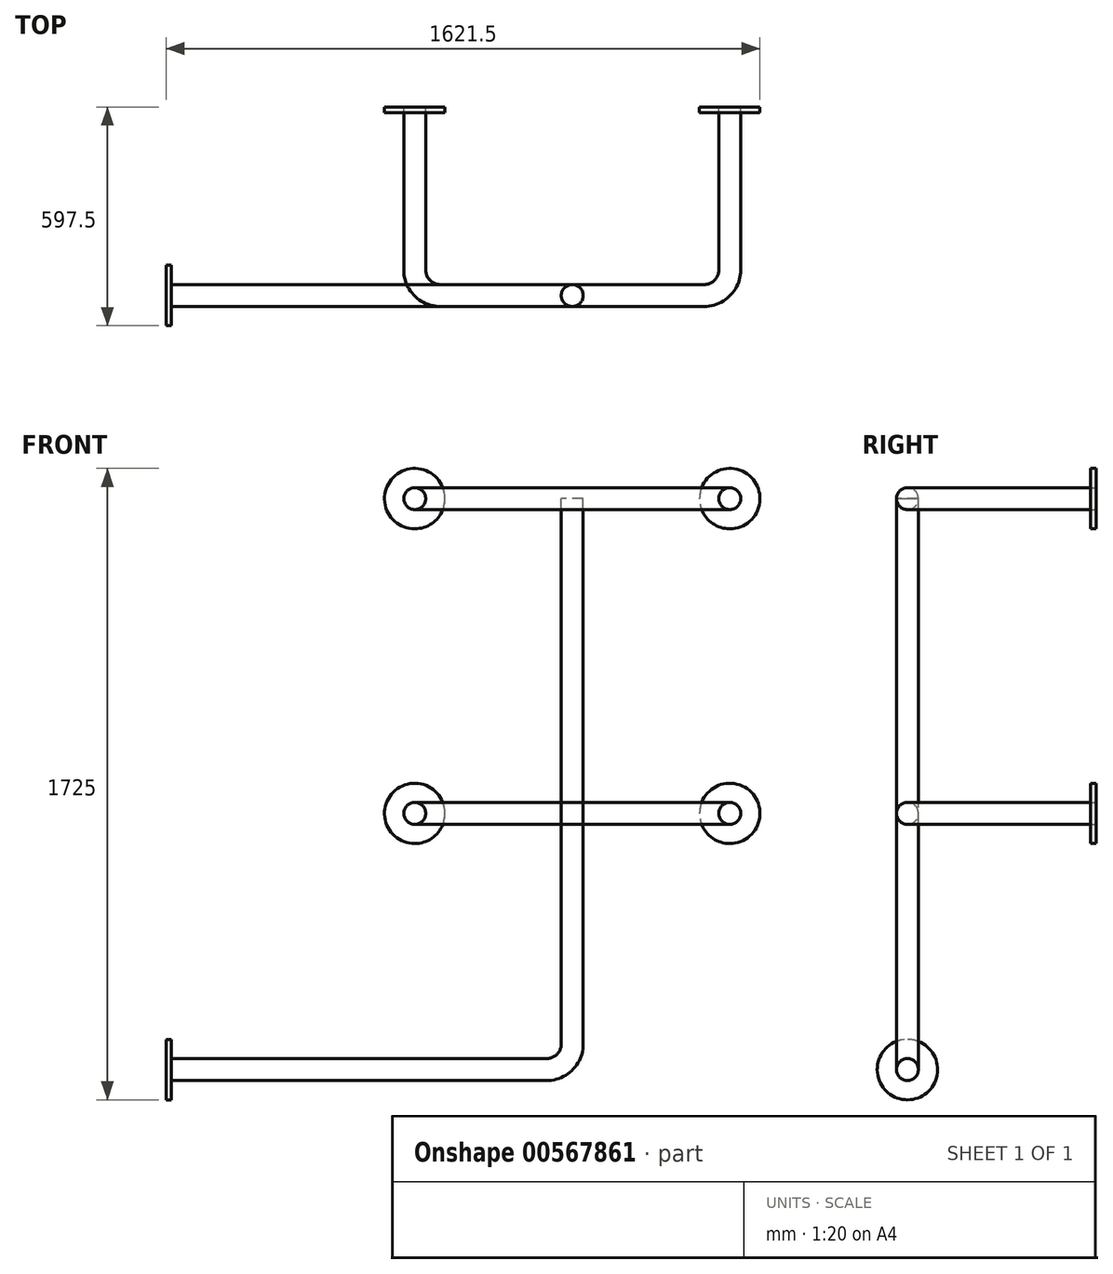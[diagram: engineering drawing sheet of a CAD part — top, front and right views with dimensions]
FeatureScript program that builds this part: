
annotation { "Feature Type Name" : "Feature", "Feature Type Description" : "" }
export const myFeature = defineFeature(function(context is Context, id is Id, definition is map)
    precondition{}
    {
        {
            var Q0;
            Q0=qCreatedBy(makeId("Front.planeOp"),FACE);
            var sketch = newSketch(context, id + "F0", { "sketchPlane" : qUnion([Q0])});
            skCircle(sketch, "E0", {"center": v(0, 0) * mm, "radius": 30 * mm});
            skCircle(sketch, "E1", {"center": v(0, 0) * mm, "radius": 82.5 * mm});
            skCircle(sketch, "E2", {"center": v(860, 0) * mm, "radius": 30 * mm});
            skCircle(sketch, "E3", {"center": v(860, 0) * mm, "radius": 82.5 * mm});
            skCircle(sketch, "E4", {"center": v(0, -860) * mm, "radius": 30 * mm});
            skCircle(sketch, "E5", {"center": v(0, -860) * mm, "radius": 82.5 * mm});
            skCircle(sketch, "E6", {"center": v(860, -860) * mm, "radius": 30 * mm});
            skCircle(sketch, "E7", {"center": v(860, -860) * mm, "radius": 82.5 * mm});
            skSolve(sketch);
        }
        {
            var Q0;
            Q0=qCreatedBy(makeId("Right.planeOp"),FACE);
            var sketch = newSketch(context, id + "F1", { "sketchPlane" : qUnion([Q0])});
            skLineSegment(sketch, "E8", {"start": v(0, 0) * mm, "end": v(-515, 0) * mm});
            skLineSegment(sketch, "E9", {"start": v(0, -860) * mm, "end": v(-515, -860) * mm});
            skSolve(sketch);
        }
        {
            var Q0;
            Q0=qCreatedBy(makeId("Right.planeOp"),FACE);
            cPlane(context, id + "F2", {"entities" : qUnion([Q0]), "cplaneType" : CPlaneType.OFFSET, "offset" : 860 * mm, "width" : 150 * mm, "height" : 150 * mm});
        }
        {
            var Q0;
            Q0=qCreatedBy(id+"F2.planeOp",FACE);
            var sketch = newSketch(context, id + "F3", { "sketchPlane" : qUnion([Q0])});
            skLineSegment(sketch, "E10", {"start": v(0, 0) * mm, "end": v(-515, 0) * mm});
            skLineSegment(sketch, "E11", {"start": v(0, -860) * mm, "end": v(-515, -860) * mm});
            skSolve(sketch);
        }
        {
            var Q0;
            Q0=qCreatedBy(makeId("Top.planeOp"),FACE);
            var sketch = newSketch(context, id + "F4", { "sketchPlane" : qUnion([Q0])});
            skLineSegment(sketch, "E12.0", {"start": v(0, 0) * mm, "end": v(0, -445) * mm});
            skLineSegment(sketch, "E13.0", {"start": v(860, 0) * mm, "end": v(860, -445) * mm});
            skLineSegment(sketch, "E14", {"start": v(70, -515) * mm, "end": v(790, -515) * mm});
            skPoint(sketch, "E15.visualSharp", {"position": v(0, -515) * mm});
            skArc(sketch, "E15.filletArc", {"start": v(0, -445) * mm, "mid": v(20.5, -494.5) * mm, "end": v(70, -515) * mm});
            skPoint(sketch, "E16.visualSharp", {"position": v(860, -515) * mm});
            skArc(sketch, "E16.filletArc", {"start": v(790, -515) * mm, "mid": v(839.5, -494.5) * mm, "end": v(860, -445) * mm});
            skSolve(sketch);
        }
        {
            var Q0;
            Q0=qCreatedBy(makeId("Top.planeOp"),FACE);
            cPlane(context, id + "F5", {"entities" : qUnion([Q0]), "cplaneType" : CPlaneType.OFFSET, "offset" : 860 * mm, "oppositeDirection" : true, "width" : 150 * mm, "height" : 150 * mm});
        }
        {
            var Q0;
            Q0=qCreatedBy(id+"F5.planeOp",FACE);
            var sketch = newSketch(context, id + "F6", { "sketchPlane" : qUnion([Q0])});
            skLineSegment(sketch, "E17.0", {"start": v(0, 0) * mm, "end": v(0, -445) * mm});
            skLineSegment(sketch, "E18.0", {"start": v(860, 0) * mm, "end": v(860, -445) * mm});
            skLineSegment(sketch, "E19", {"start": v(70, -515) * mm, "end": v(790, -515) * mm});
            skPoint(sketch, "E20.visualSharp", {"position": v(0, -515) * mm});
            skArc(sketch, "E20.filletArc", {"start": v(0, -445) * mm, "mid": v(20.5, -494.5) * mm, "end": v(70, -515) * mm});
            skPoint(sketch, "E21.visualSharp", {"position": v(860, -515) * mm});
            skArc(sketch, "E21.filletArc", {"start": v(790, -515) * mm, "mid": v(839.5, -494.5) * mm, "end": v(860, -445) * mm});
            skSolve(sketch);
        }
        {
            var Q0;
            Q0=qCreatedBy(makeId("Front.planeOp"),FACE);
            cPlane(context, id + "F7", {"entities" : qUnion([Q0]), "cplaneType" : CPlaneType.OFFSET, "offset" : 515 * mm, "width" : 150 * mm, "height" : 150 * mm});
        }
        {
            var Q0;
            Q0=qCreatedBy(id+"F7.planeOp",FACE);
            var sketch = newSketch(context, id + "F8", { "sketchPlane" : qUnion([Q0])});
            skLineSegment(sketch, "E22.0", {"start": v(70, 0) * mm, "end": v(790, 0) * mm});
            skLineSegment(sketch, "E23.0", {"start": v(70, -860) * mm, "end": v(790, -860) * mm});
            skLineSegment(sketch, "E24", {"start": v(430, 0) * mm, "end": v(430, -860) * mm});
            skLineSegment(sketch, "E25", {"start": v(430, -860) * mm, "end": v(430, -1490) * mm});
            skLineSegment(sketch, "E26", {"start": v(360, -1560) * mm, "end": v(-679, -1560) * mm});
            skPoint(sketch, "E27.visualSharp", {"position": v(430, -1560) * mm});
            skArc(sketch, "E27.filletArc", {"start": v(360, -1560) * mm, "mid": v(409.5, -1539.5) * mm, "end": v(430, -1490) * mm});
            skSolve(sketch);
        }
        {
            var Q0;
            Q0=qCreatedBy(makeId("Right.planeOp"),FACE);
            cPlane(context, id + "F9", {"entities" : qUnion([Q0]), "cplaneType" : CPlaneType.OFFSET, "offset" : 679 * mm, "oppositeDirection" : true, "width" : 150 * mm, "height" : 150 * mm});
        }
        {
            var Q0;
            Q0=qCreatedBy(id+"F9.planeOp",FACE);
            var sketch = newSketch(context, id + "F10", { "sketchPlane" : qUnion([Q0])});
            skPoint(sketch, "E28.0", {"position": v(-515, -1560) * mm});
            skCircle(sketch, "E29", {"center": v(-515, -1560) * mm, "radius": 30 * mm});
            skCircle(sketch, "E30", {"center": v(-515, -1560) * mm, "radius": 82.5 * mm});
            skSolve(sketch);
        }
        {
            var Q0;
            Q0=makeQuery(id+"F0.imprint","IMPRINT",FACE,{"disambiguationData":[TD([[makeQuery(id+"F0.imprint","IMPRINT",EDGE,{"derivedFrom":sQuery(id+"F0.wireOp",EDGE,"E0")}),1.0]])]});
            var Q1;
            Q1=sQuery(id+"F4.wireOp",EDGE,"E12.0");
            var Q2;
            Q2=sQuery(id+"F4.wireOp",EDGE,"E15.filletArc");
            var Q3;
            Q3=sQuery(id+"F8.wireOp",EDGE,"E22.0");
            var Q4;
            Q4=sQuery(id+"F4.wireOp",EDGE,"E16.filletArc");
            var Q5;
            Q5=sQuery(id+"F4.wireOp",EDGE,"E13.0");
            sweep(context, id + "F11", {"profiles" : qUnion([Q0]), "path" : qUnion([Q1, Q2, Q3, Q4, Q5])});
        }
        {
            var Q0;
            Q0=makeQuery(id+"F0.imprint","IMPRINT",FACE,{"disambiguationData":[TD([[makeQuery(id+"F0.imprint","IMPRINT",EDGE,{"derivedFrom":sQuery(id+"F0.wireOp",EDGE,"E6")}),1.0]])]});
            var Q1;
            Q1=sQuery(id+"F6.wireOp",EDGE,"E18.0");
            var Q2;
            Q2=sQuery(id+"F6.wireOp",EDGE,"E21.filletArc");
            var Q3;
            Q3=sQuery(id+"F8.wireOp",EDGE,"E23.0");
            var Q4;
            Q4=sQuery(id+"F6.wireOp",EDGE,"E20.filletArc");
            var Q5;
            Q5=sQuery(id+"F6.wireOp",EDGE,"E17.0");
            sweep(context, id + "F12", {"profiles" : qUnion([Q0]), "path" : qUnion([Q1, Q2, Q3, Q4, Q5])});
        }
        {
            var Q0;
            Q0=makeQuery(id+"F10.imprint","IMPRINT",FACE,{"disambiguationData":[TD([[makeQuery(id+"F10.imprint","IMPRINT",EDGE,{"derivedFrom":sQuery(id+"F10.wireOp",EDGE,"E29")}),1.0]])]});
            var Q1;
            Q1=sQuery(id+"F8.wireOp",EDGE,"E26");
            var Q2;
            Q2=sQuery(id+"F8.wireOp",EDGE,"E27.filletArc");
            var Q3;
            Q3=sQuery(id+"F8.wireOp",EDGE,"E25");
            var Q4;
            Q4=sQuery(id+"F8.wireOp",EDGE,"E24");
            sweep(context, id + "F13", {"profiles" : qUnion([Q0]), "path" : qUnion([Q1, Q2, Q3, Q4])});
        }
        {
            var Q0;
            Q0=makeQuery(id+"F0.imprint","IMPRINT",FACE,{"disambiguationData":[TD([[makeQuery(id+"F0.imprint","IMPRINT",EDGE,{"derivedFrom":sQuery(id+"F0.wireOp",EDGE,"E0")}),-1.0]])]});
            var Q1;
            Q1=makeQuery(id+"F0.imprint","IMPRINT",FACE,{"disambiguationData":[TD([[makeQuery(id+"F0.imprint","IMPRINT",EDGE,{"derivedFrom":sQuery(id+"F0.wireOp",EDGE,"E2")}),-1.0]])]});
            var Q2;
            Q2=makeQuery(id+"F0.imprint","IMPRINT",FACE,{"disambiguationData":[TD([[makeQuery(id+"F0.imprint","IMPRINT",EDGE,{"derivedFrom":sQuery(id+"F0.wireOp",EDGE,"E4")}),-1.0]])]});
            var Q3;
            Q3=makeQuery(id+"F0.imprint","IMPRINT",FACE,{"disambiguationData":[TD([[makeQuery(id+"F0.imprint","IMPRINT",EDGE,{"derivedFrom":sQuery(id+"F0.wireOp",EDGE,"E6")}),-1.0]])]});
            var Q4;
            Q4=sQuery(id+"F0.wireOp",EDGE,"E1");
            var Q5;
            Q5=sQuery(id+"F0.wireOp",EDGE,"E3");
            var Q6;
            Q6=sQuery(id+"F0.wireOp",EDGE,"E5");
            var Q7;
            Q7=sQuery(id+"F0.wireOp",EDGE,"E7");
            extrude(context, id + "F14", {"entities" : qUnion([Q0, Q1, Q2, Q3]), "surfaceEntities" : qUnion([Q4, Q5, Q6, Q7]), "depth" : 15 * mm, "offsetDistance" : 25 * mm});
        }
        {
            var Q0;
            Q0=makeQuery(id+"F10.imprint","IMPRINT",FACE,{"disambiguationData":[TD([[makeQuery(id+"F10.imprint","IMPRINT",EDGE,{"derivedFrom":sQuery(id+"F10.wireOp",EDGE,"E29")}),-1.0]])]});
            extrude(context, id + "F15", {"entities" : qUnion([Q0]), "operationType" : NewBodyOperationType.ADD, "depth" : 15 * mm, "offsetDistance" : 25 * mm});
        }
    });
